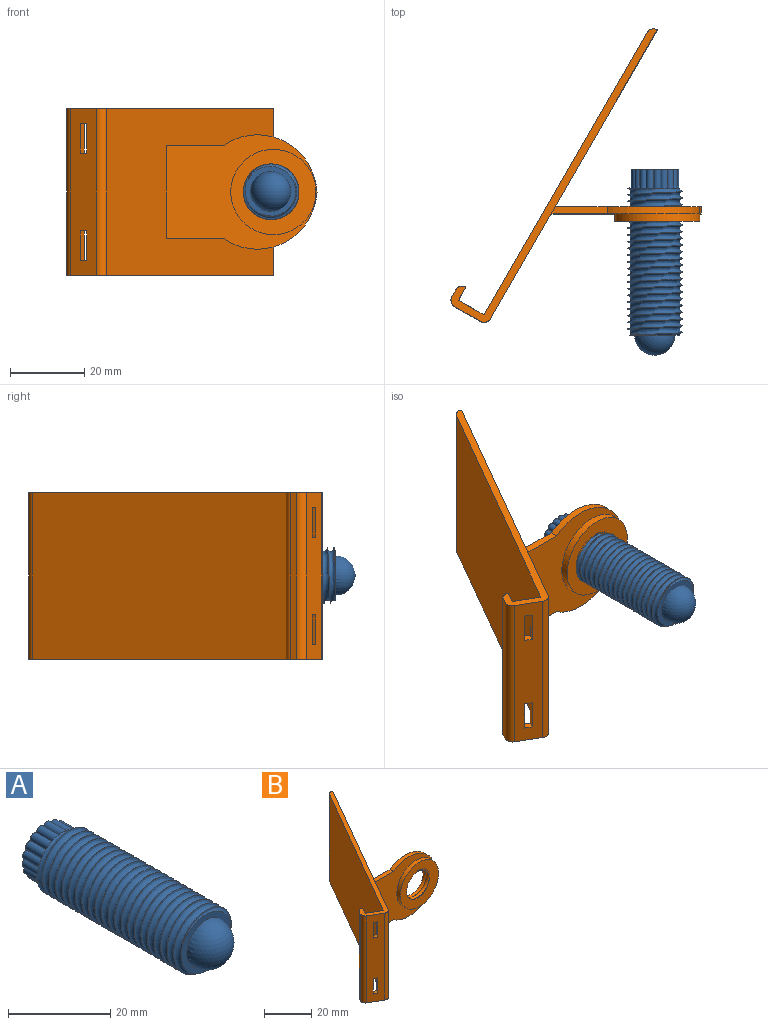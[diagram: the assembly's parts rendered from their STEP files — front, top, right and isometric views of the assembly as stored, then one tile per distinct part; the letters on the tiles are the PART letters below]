
ASSEMBLY  parts=2 mates=1
PART A: 24 faces, bbox 47.6x79.5x48.5 mm
  f0: cylinder r=7.5mm len=39.7mm, axis (0,1,0), area 15.1mm2, adj f1,f2,f3
  f1: bspline ~45.3x19.1mm, area 2329.4mm2, adj f0,f2,f3
  f2: plane 43.06x42.9mm, normal (0,-1,0), area 53.3mm2, adj f0,f1,f4
  f3: plane 43.45x42.86mm, normal (0,1,0), area 23.6mm2, adj f0,f1,f5,f7,f8,f9,f10,f11
  f4: sphere r=5.41mm, area 184mm2, adj f2
  f5: cylinder r=1mm len=5mm, axis (0,-1,0), area 14.1mm2, adj f3,f6,f7,f8
  f6: plane 12.82x12.81mm, normal (0,1,0), area 121.7mm2, adj f5,f7,f8,f9,f10,f11,f12,f13
  f7: cylinder r=1mm len=5mm, axis (0,-1,0), area 14.1mm2, adj f3,f5,f6,f9
  f8: cylinder r=1mm len=5mm, axis (0,-1,0), area 14.1mm2, adj f3,f5,f6,f16
  f9: cylinder r=1mm len=5mm, axis (0,-1,0), area 14.1mm2, adj f3,f6,f7,f10
  f10: cylinder r=1mm len=5mm, axis (0,-1,0), area 14.1mm2, adj f3,f6,f9,f11
  f11: cylinder r=1mm len=5mm, axis (0,-1,0), area 14.1mm2, adj f3,f6,f10,f12
  f12: cylinder r=1mm len=5mm, axis (0,-1,0), area 14.1mm2, adj f3,f6,f11,f13
  f13: cylinder r=1mm len=5mm, axis (0,-1,0), area 14.1mm2, adj f3,f6,f12,f14
  f14: cylinder r=1mm len=5mm, axis (0,-1,0), area 14.1mm2, adj f3,f6,f13,f15
  f15: cylinder r=1mm len=5mm, axis (0,-1,0), area 14.1mm2, adj f3,f6,f14,f23
  f16: cylinder r=1mm len=5mm, axis (0,-1,0), area 14.1mm2, adj f3,f6,f8,f17
  f17: cylinder r=1mm len=5mm, axis (0,-1,0), area 14.1mm2, adj f3,f6,f16,f18
  f18: cylinder r=1mm len=5mm, axis (0,-1,0), area 14.1mm2, adj f3,f6,f17,f19
  f19: cylinder r=1mm len=5mm, axis (0,-1,0), area 14.1mm2, adj f3,f6,f18,f20
  f20: cylinder r=1mm len=5mm, axis (0,-1,0), area 14.1mm2, adj f3,f6,f19,f21
  f21: cylinder r=1mm len=5mm, axis (0,-1,0), area 14.1mm2, adj f3,f6,f20,f22
  f22: cylinder r=1mm len=5mm, axis (0,-1,0), area 14.1mm2, adj f3,f6,f21,f23
  f23: cylinder r=1mm len=5mm, axis (0,-1,0), area 14.1mm2, adj f3,f6,f15,f22
PART B: 33 faces, bbox 71.1x82.8x48.6 mm
  f0: plane 45x6.93mm, normal (0.5,0.87,0), area 328mm2, adj f1,f22,f23,f24,f25,f26,f27,f28
  f1: plane 2.73x2.73mm, normal (0,0,1), area 4mm2, adj f0,f2,f22,f24
  f2: plane 45x6.93mm, normal (-0.5,-0.87,0), area 328mm2, adj f1,f3,f19,f22,f23,f24,f26,f28
  f3: cylinder r=2mm len=45mm, axis (0,0,-1), area 141.4mm2, adj f2,f4,f26,f28
  f4: plane 77.93x45mm, normal (0.87,-0.5,0), area 3991.6mm2, adj f3,f5,f15,f16,f17,f18,f26,f28
  f5: plane 39.34x30.89mm, normal (0,1,0), area 856.4mm2, adj f4,f6,f7,f8,f9,f10,f11,f15
  f6: cylinder r=16mm len=24.86mm, axis (0,1,0), area 63mm2, adj f5,f7,f16,f17
  f7: cylinder r=25mm len=2.87mm, axis (0,1,0), area 5.8mm2, adj f5,f6,f8,f16
  f8: cylinder r=25mm len=2.87mm, axis (0,-1,0), area 5.8mm2, adj f5,f7,f9,f16
  f9: cylinder r=16mm len=24.86mm, axis (0,1,0), area 63mm2, adj f5,f8,f15,f16
  f10: bspline ~19.1x18.23mm, area 3mm2, adj f5,f11
  f11: cylinder r=7.5mm len=15mm, axis (0,1,0), area 1.4mm2, adj f5,f10,f12,f13
  f12: bspline ~16.79x16.79mm, area 240.1mm2, adj f11,f13
  f13: plane 26.6x26.6mm, normal (0,-1,0), area 270.2mm2, adj f11,f12,f14
  f14: cylinder r=11.5mm len=23mm, axis (0,1,0), area 144.5mm2, adj f13,f16
  f15: plane 15.15x2mm, normal (0,0,1), area 29.2mm2, adj f4,f5,f9,f16
  f16: plane 40.47x30.87mm, normal (0,-1,0), area 615.2mm2, adj f4,f6,f7,f8,f9,f14,f15,f17
  f17: plane 15.15x2mm, normal (0,0,-1), area 29.2mm2, adj f4,f5,f6,f16
  f18: cylinder r=2mm len=45mm, axis (0,0,1), area 141.4mm2, adj f4,f25,f26,f28
  f19: cylinder r=2mm len=45mm, axis (0,0,-1), area 141.4mm2, adj f2,f20,f26,f28
  f20: plane 45x1.73mm, normal (-0.87,0.5,0), area 90mm2, adj f19,f21,f26,f28
  f21: cylinder r=2mm len=45mm, axis (0,0,-1), area 141.4mm2, adj f20,f26,f27,f28
  f22: plane 8x1.73mm, normal (0.87,-0.5,0), area 16mm2, adj f0,f1,f2,f23
  f23: plane 2.73x2.73mm, normal (0,0,-1), area 4mm2, adj f0,f2,f22,f24
  f24: plane 8x1.73mm, normal (-0.87,0.5,0), area 16mm2, adj f0,f1,f2,f23
  f25: plane 76.2x45mm, normal (-0.87,0.5,0), area 3959.4mm2, adj f0,f18,f26,f28
  f26: plane 79.2x55.65mm, normal (0,0,1), area 208.5mm2, adj f0,f2,f3,f4,f18,f19,f20,f21
  f27: plane 45x3.46mm, normal (0.87,-0.5,0), area 180mm2, adj f0,f21,f26,f28
  f28: plane 79.2x55.65mm, normal (0,0,-1), area 208.5mm2, adj f0,f2,f3,f4,f18,f19,f20,f21
  f29: plane 2.73x2.73mm, normal (0,0,1), area 4mm2, adj f0,f2,f30,f32
  f30: plane 8x1.73mm, normal (0.87,-0.5,0), area 16mm2, adj f0,f2,f29,f31
  f31: plane 2.73x2.73mm, normal (0,0,-1), area 4mm2, adj f0,f2,f30,f32
  f32: plane 8x1.73mm, normal (-0.87,0.5,0), area 16mm2, adj f0,f2,f29,f31
PLACE A t=(-29.62,-5,22.87)mm
PLACE B t=(-29.9,0,22.8)mm
MATE cylindrical A.f0 <-> B.f5  axis (0,1,0) through (-24.46,39.27,45.37)mm
